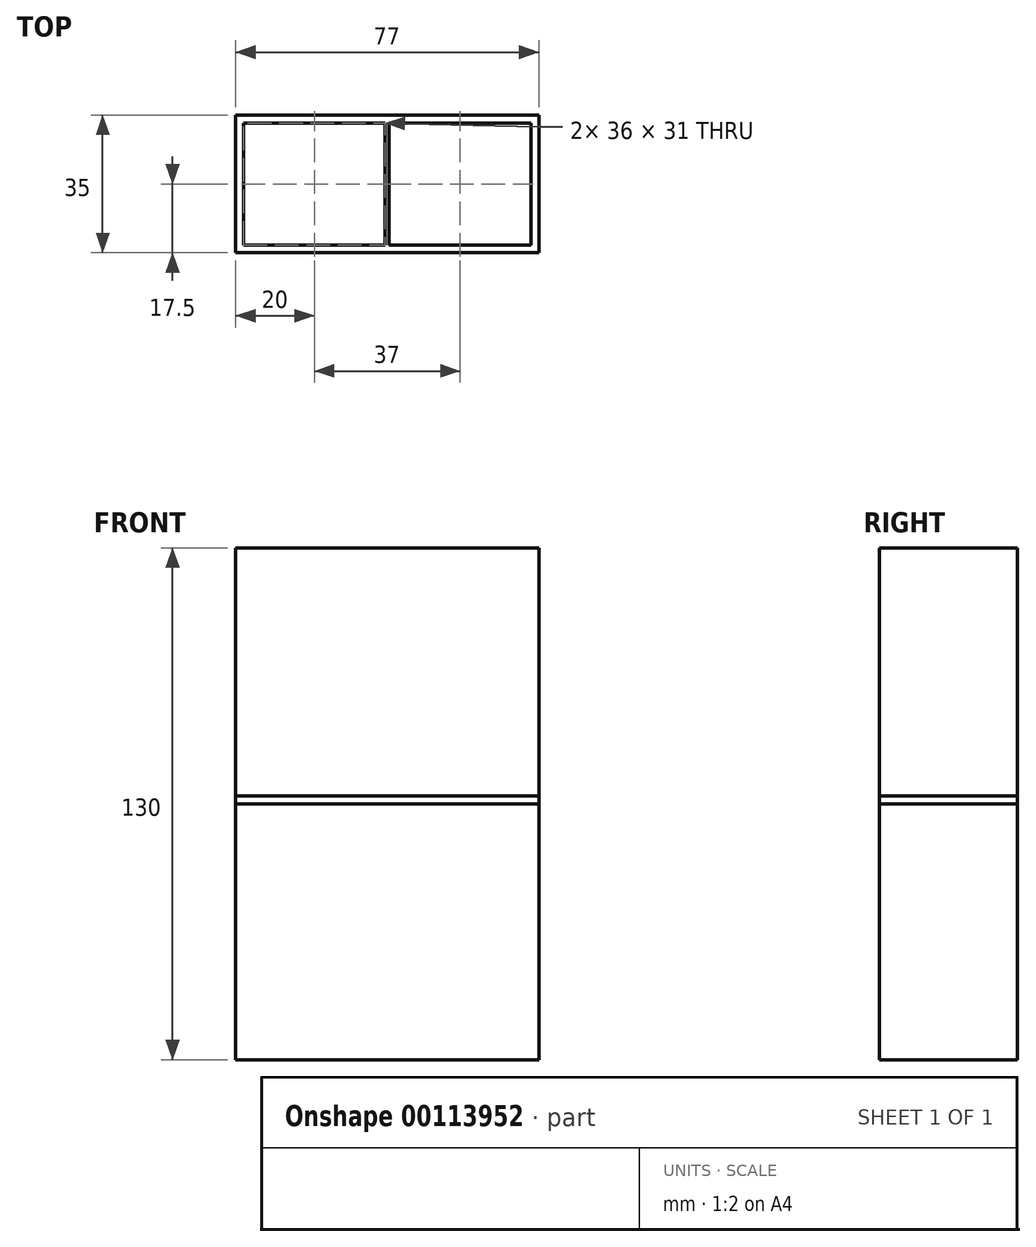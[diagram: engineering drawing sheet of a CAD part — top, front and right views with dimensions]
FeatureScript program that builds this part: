
annotation { "Feature Type Name" : "Feature", "Feature Type Description" : "" }
export const myFeature = defineFeature(function(context is Context, id is Id, definition is map)
    precondition{}
    {
        {
            var Q0;
            Q0=qCreatedBy(makeId("Top.planeOp"),FACE);
            var sketch = newSketch(context, id + "F0", { "sketchPlane" : qUnion([Q0])});
            skLineSegment(sketch, "E0.bottom", {"start": v(38.5, -17.5) * mm, "end": v(-38.5, -17.5) * mm});
            skLineSegment(sketch, "E0.top", {"start": v(38.5, 17.5) * mm, "end": v(-38.5, 17.5) * mm});
            skLineSegment(sketch, "E0.left", {"start": v(38.5, -17.5) * mm, "end": v(38.5, 17.5) * mm});
            skLineSegment(sketch, "E0.right", {"start": v(-38.5, -17.5) * mm, "end": v(-38.5, 17.5) * mm});
            skPoint(sketch, "E0.middle", {"position": v(0, 0) * mm});
            skLineSegment(sketch, "E1.bottom", {"start": v(-0.5, -15.5) * mm, "end": v(-36.5, -15.5) * mm});
            skLineSegment(sketch, "E1.top", {"start": v(-0.5, 15.5) * mm, "end": v(-36.5, 15.5) * mm});
            skLineSegment(sketch, "E1.left", {"start": v(-0.5, -15.5) * mm, "end": v(-0.5, 15.5) * mm});
            skLineSegment(sketch, "E1.right", {"start": v(-36.5, -15.5) * mm, "end": v(-36.5, 15.5) * mm});
            skPoint(sketch, "E1.middle", {"position": v(-18.5, 0) * mm});
            skLineSegment(sketch, "E2.bottom", {"start": v(36.5, -15.5) * mm, "end": v(0.5, -15.5) * mm});
            skLineSegment(sketch, "E2.top", {"start": v(36.5, 15.5) * mm, "end": v(0.5, 15.5) * mm});
            skLineSegment(sketch, "E2.left", {"start": v(36.5, -15.5) * mm, "end": v(36.5, 15.5) * mm});
            skLineSegment(sketch, "E2.right", {"start": v(0.5, -15.5) * mm, "end": v(0.5, 15.5) * mm});
            skPoint(sketch, "E2.middle", {"position": v(18.5, 0) * mm});
            skPoint(sketch, "E2.middle.positionSnap0", {"position": v(38.5, 0) * mm});
            skPoint(sketch, "E2.centerSnap0", {"position": v(38.5, 0) * mm});
            skSolve(sketch);
        }
        {
            var Q0;
            Q0=makeQuery(id+"F0.imprint","IMPRINT",FACE,{"disambiguationData":[TD([[makeQuery(id+"F0.imprint","IMPRINT",EDGE,{"derivedFrom":sQuery(id+"F0.wireOp",EDGE,"E0.bottom")}),-1.0]])]});
            extrude(context, id + "F1", {"entities" : qUnion([Q0]), "endBound" : BoundingType.SYMMETRIC, "depth" : 130 * mm});
        }
        {
            var Q0;
            Q0=makeQuery(id+"F0.imprint","IMPRINT",FACE,{"disambiguationData":[TD([[makeQuery(id+"F0.imprint","IMPRINT",EDGE,{"derivedFrom":sQuery(id+"F0.wireOp",EDGE,"E0.bottom")}),-1.0]])]});
            var Q1;
            Q1=makeQuery(id+"F0.imprint","IMPRINT",FACE,{"disambiguationData":[TD([[makeQuery(id+"F0.imprint","IMPRINT",EDGE,{"derivedFrom":sQuery(id+"F0.wireOp",EDGE,"E2.bottom")}),-1.0]])]});
            var Q2;
            Q2=makeQuery(id+"F0.imprint","IMPRINT",FACE,{"disambiguationData":[TD([[makeQuery(id+"F0.imprint","IMPRINT",EDGE,{"derivedFrom":sQuery(id+"F0.wireOp",EDGE,"E1.bottom")}),-1.0]])]});
            extrude(context, id + "F2", {"entities" : qUnion([Q0, Q1, Q2]), "depth" : 2 * mm});
        }
    });
